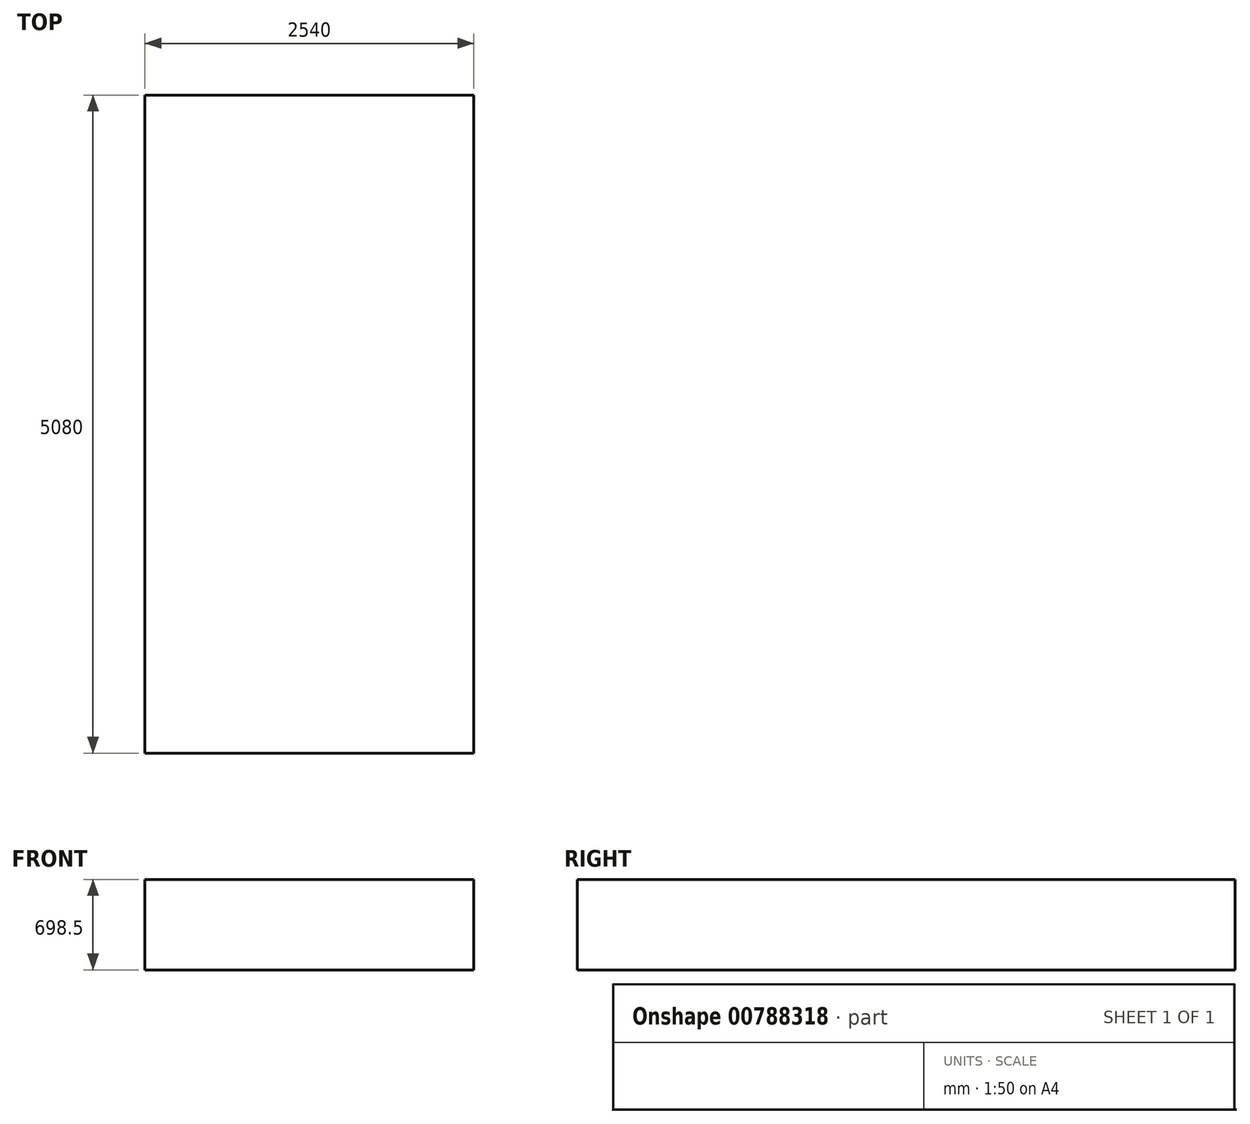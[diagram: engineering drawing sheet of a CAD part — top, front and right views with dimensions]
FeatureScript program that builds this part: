
annotation { "Feature Type Name" : "Feature", "Feature Type Description" : "" }
export const myFeature = defineFeature(function(context is Context, id is Id, definition is map)
    precondition{}
    {
        {
            var Q0;
            Q0=qCreatedBy(makeId("Top.planeOp"),FACE);
            var sketch = newSketch(context, id + "F0", { "sketchPlane" : qUnion([Q0])});
            skLineSegment(sketch, "E0.bottom", {"start": v(2454.42, 5047.64) * mm, "end": v(-85.58, 5047.64) * mm});
            skLineSegment(sketch, "E0.top", {"start": v(2454.42, -32.36) * mm, "end": v(-85.58, -32.36) * mm});
            skLineSegment(sketch, "E0.left", {"start": v(2454.42, 5047.64) * mm, "end": v(2454.42, -32.36) * mm});
            skLineSegment(sketch, "E0.right", {"start": v(-85.58, 5047.64) * mm, "end": v(-85.58, -32.36) * mm});
            skSolve(sketch);
        }
        {
            var Q0;
            Q0=makeQuery(id+"F0.imprint","IMPRINT",FACE,{"disambiguationData":[TD([[makeQuery(id+"F0.imprint","IMPRINT",EDGE,{"derivedFrom":sQuery(id+"F0.wireOp",EDGE,"E0.bottom")}),1.0]])]});
            extrude(context, id + "F1", {"entities" : qUnion([Q0]), "depth" : 698.5 * mm, "offsetDistance" : 25.4 * mm});
        }
    });
